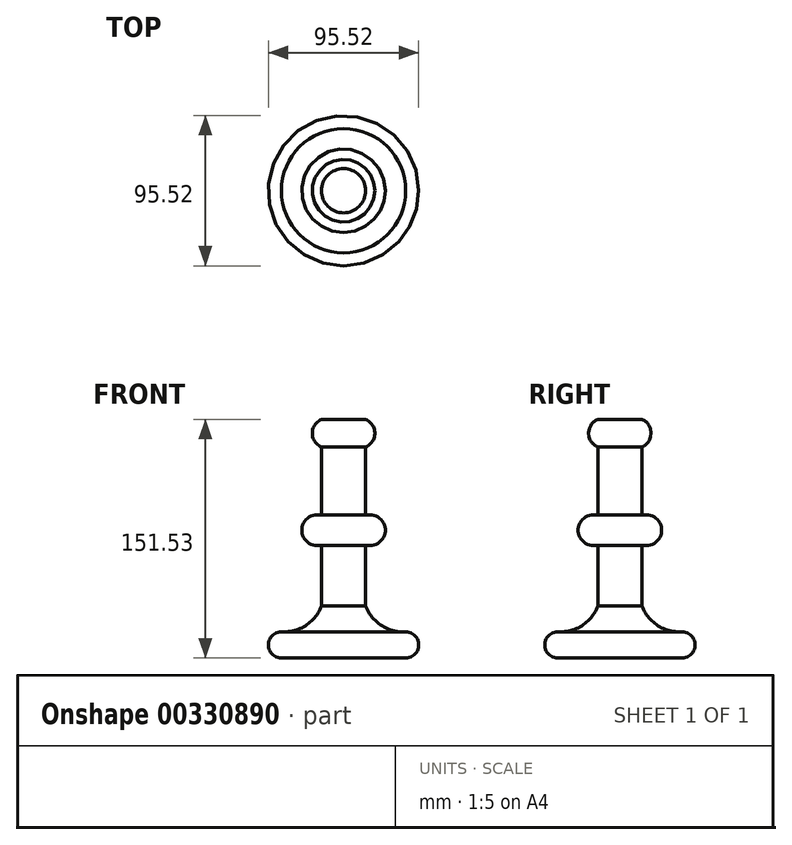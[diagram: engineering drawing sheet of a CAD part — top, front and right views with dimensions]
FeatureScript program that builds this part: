
annotation { "Feature Type Name" : "Feature", "Feature Type Description" : "" }
export const myFeature = defineFeature(function(context is Context, id is Id, definition is map)
    precondition{}
    {
        {
            var Q0;
            Q0=qCreatedBy(makeId("Front.planeOp"),FACE);
            var sketch = newSketch(context, id + "F0", { "sketchPlane" : qUnion([Q0])});
            skLineSegment(sketch, "E0", {"start": v(0, 0) * mm, "end": v(39.45, 0) * mm});
            skArc(sketch, "E1", {"start": v(39.45, 0) * mm, "mid": v(47.76, 8.3) * mm, "end": v(39.45, 16.62) * mm});
            skArc(sketch, "E2", {"start": v(14.02, 33.09) * mm, "mid": v(24, 20.65) * mm, "end": v(39.45, 16.62) * mm});
            skLineSegment(sketch, "E3", {"start": v(14.02, 33.09) * mm, "end": v(14.02, 71.81) * mm});
            skArc(sketch, "E4", {"start": v(14.02, 71.81) * mm, "mid": v(26.53, 81.18) * mm, "end": v(14.02, 90.55) * mm});
            skLineSegment(sketch, "E5", {"start": v(14.02, 90.55) * mm, "end": v(14.02, 134.02) * mm});
            skArc(sketch, "E6", {"start": v(14.02, 134.02) * mm, "mid": v(19.86, 142.78) * mm, "end": v(14.02, 151.53) * mm});
            skLineSegment(sketch, "E7", {"start": v(14.02, 151.53) * mm, "end": v(0, 151.53) * mm});
            skLineSegment(sketch, "E8", {"start": v(0, 151.53) * mm, "end": v(0, 0) * mm});
            skSolve(sketch);
        }
        {
            var Q0;
            Q0=makeQuery(id+"F0.imprint","IMPRINT",FACE,{"disambiguationData":[TD([[makeQuery(id+"F0.imprint","IMPRINT",EDGE,{"derivedFrom":sQuery(id+"F0.wireOp",EDGE,"E0")}),1.0]])]});
            var Q1;
            Q1=sQuery(id+"F0.wireOp",EDGE,"E8");
            revolve(context, id + "F1", {"entities" : qUnion([Q0]), "axis" : qUnion([Q1]), "revolveType" : RevolveType.FULL});
        }
    });
